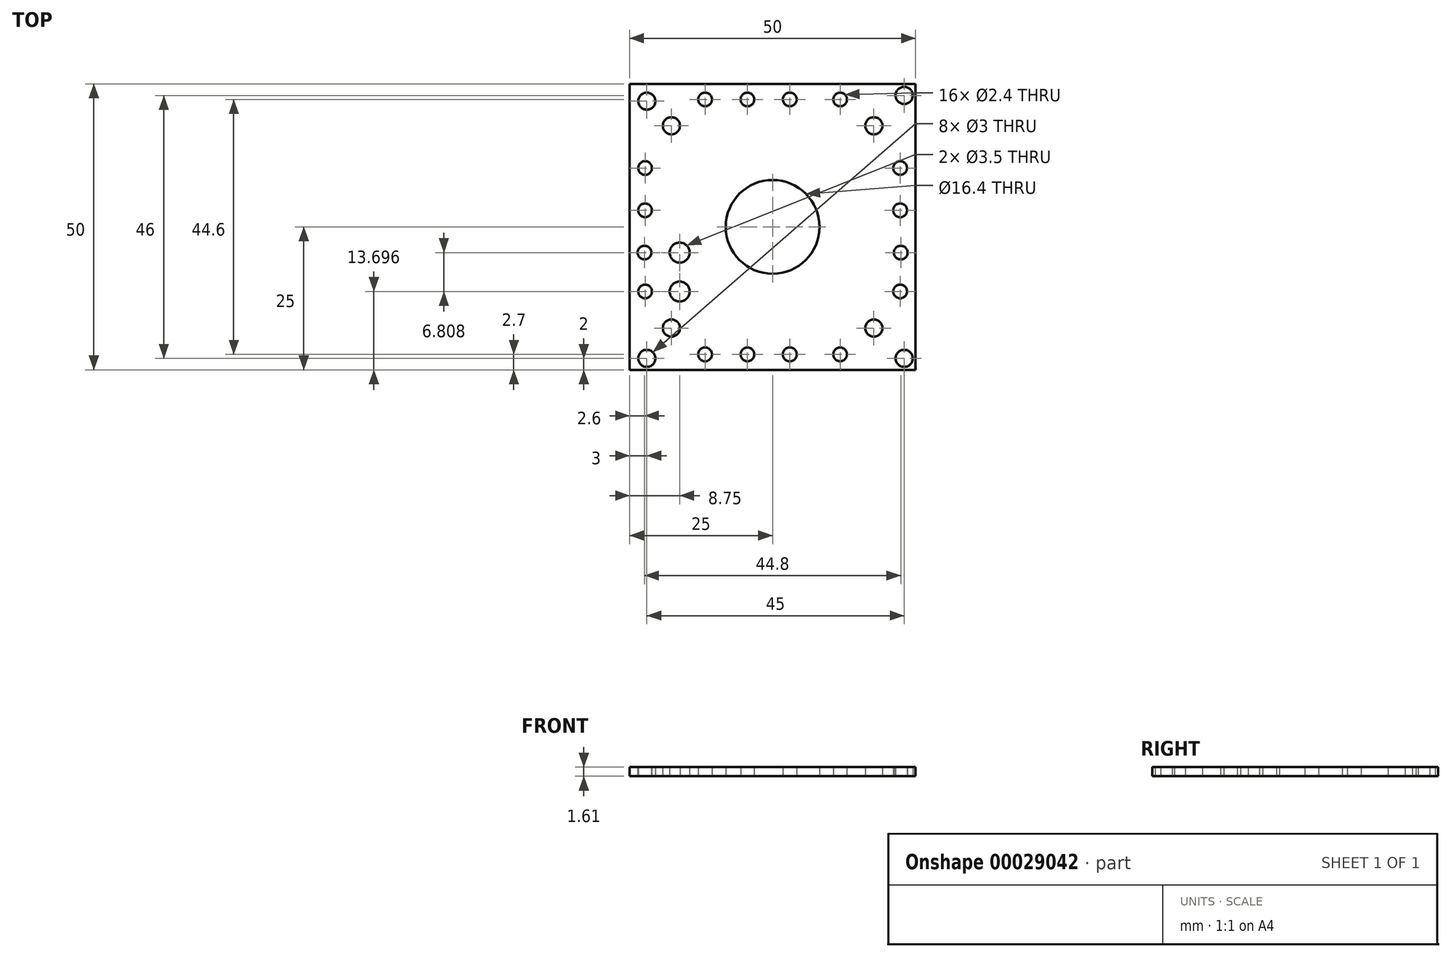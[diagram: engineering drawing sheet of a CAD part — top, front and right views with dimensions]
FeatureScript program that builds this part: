
annotation { "Feature Type Name" : "Feature", "Feature Type Description" : "" }
export const myFeature = defineFeature(function(context is Context, id is Id, definition is map)
    precondition{}
    {
        {
            var Q0;
            Q0=qCreatedBy(makeId("Top.planeOp"),FACE);
            var sketch = newSketch(context, id + "F0", { "sketchPlane" : qUnion([Q0])});
            skLineSegment(sketch, "E0.rect.bottom", {"start": v(-25, 25) * mm, "end": v(25, 25) * mm});
            skLineSegment(sketch, "E0.rect.top", {"start": v(-25, -25) * mm, "end": v(25, -25) * mm});
            skLineSegment(sketch, "E0.rect.left", {"start": v(-25, 25) * mm, "end": v(-25, -25) * mm});
            skLineSegment(sketch, "E0.rect.right", {"start": v(25, 25) * mm, "end": v(25, -25) * mm});
            skPoint(sketch, "E0.rect.middle", {"position": v(0, 0) * mm});
            skCircle(sketch, "E1", {"center": v(0, 0) * mm, "radius": 8.2 * mm});
            skCircle(sketch, "E2", {"center": v(-22, 22) * mm, "radius": 1.5 * mm});
            skCircle(sketch, "E3", {"center": v(23, 23) * mm, "radius": 1.5 * mm});
            skCircle(sketch, "E4", {"center": v(-22, -23) * mm, "radius": 1.5 * mm});
            skCircle(sketch, "E5", {"center": v(23, -23) * mm, "radius": 1.5 * mm});
            skCircle(sketch, "E6", {"center": v(-17.7, 17.7) * mm, "radius": 1.5 * mm});
            skCircle(sketch, "E7", {"center": v(17.7, 17.7) * mm, "radius": 1.5 * mm});
            skCircle(sketch, "E8", {"center": v(-17.7, -17.7) * mm, "radius": 1.5 * mm});
            skCircle(sketch, "E9", {"center": v(17.7, -17.7) * mm, "radius": 1.5 * mm});
            skCircle(sketch, "E10", {"center": v(-22.3, 10.3) * mm, "radius": 1.2 * mm});
            skCircle(sketch, "E11", {"center": v(-22.3, 2.9) * mm, "radius": 1.2 * mm});
            skCircle(sketch, "E12", {"center": v(-22.4, -4.5) * mm, "radius": 1.2 * mm});
            skCircle(sketch, "E13", {"center": v(-22.3, -11.3) * mm, "radius": 1.2 * mm});
            skCircle(sketch, "E14", {"center": v(-16.25, -4.5) * mm, "radius": 1.75 * mm});
            skCircle(sketch, "E15", {"center": v(-16.25, -11.3) * mm, "radius": 1.75 * mm});
            skCircle(sketch, "E16", {"center": v(-11.8, 22.3) * mm, "radius": 1.2 * mm});
            skCircle(sketch, "E17", {"center": v(-4.4, 22.3) * mm, "radius": 1.2 * mm});
            skCircle(sketch, "E18", {"center": v(3, 22.3) * mm, "radius": 1.2 * mm});
            skCircle(sketch, "E19", {"center": v(11.8, 22.3) * mm, "radius": 1.2 * mm});
            skCircle(sketch, "E20.MirrorC", {"center": v(22.3, 10.3) * mm, "radius": 1.2 * mm});
            skCircle(sketch, "E21.MirrorC", {"center": v(22.3, 2.9) * mm, "radius": 1.2 * mm});
            skCircle(sketch, "E22.MirrorC", {"center": v(22.4, -4.5) * mm, "radius": 1.2 * mm});
            skCircle(sketch, "E23.MirrorC", {"center": v(22.3, -11.3) * mm, "radius": 1.2 * mm});
            skCircle(sketch, "E24.MirrorC", {"center": v(3, -22.3) * mm, "radius": 1.2 * mm});
            skCircle(sketch, "E25.MirrorC", {"center": v(-4.4, -22.3) * mm, "radius": 1.2 * mm});
            skCircle(sketch, "E26.MirrorC", {"center": v(-11.8, -22.3) * mm, "radius": 1.2 * mm});
            skCircle(sketch, "E27.MirrorC", {"center": v(11.8, -22.3) * mm, "radius": 1.2 * mm});
            skSolve(sketch);
        }
        {
            var Q0;
            Q0=makeQuery(id+"F0.imprint","IMPRINT",FACE,{"disambiguationData":[TD([[makeQuery(id+"F0.imprint","IMPRINT",EDGE,{"derivedFrom":sQuery(id+"F0.wireOp",EDGE,"E0.rect.bottom")}),-1.0]])]});
            extrude(context, id + "F1", {"entities" : qUnion([Q0]), "depth" : 1.61 * mm});
        }
    });
